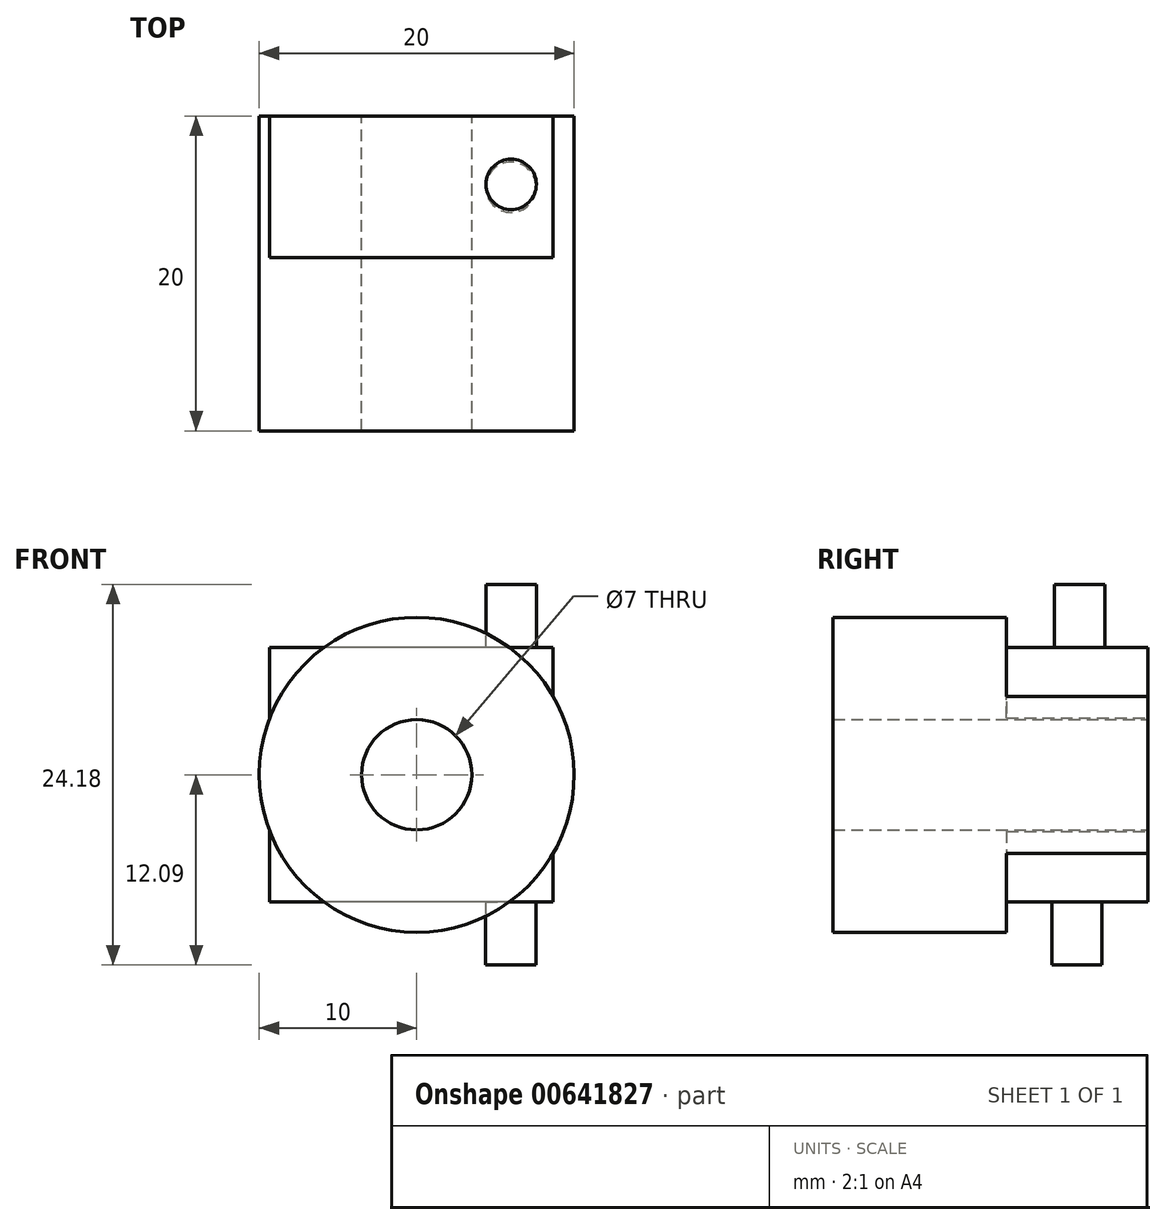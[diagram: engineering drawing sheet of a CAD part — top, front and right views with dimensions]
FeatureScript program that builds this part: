
annotation { "Feature Type Name" : "Feature", "Feature Type Description" : "" }
export const myFeature = defineFeature(function(context is Context, id is Id, definition is map)
    precondition{}
    {
        {
            var Q0;
            Q0=qCreatedBy(makeId("Front.planeOp"),FACE);
            var sketch = newSketch(context, id + "F0", { "sketchPlane" : qUnion([Q0])});
            skCircle(sketch, "E0", {"center": v(0, 0) * mm, "radius": 10 * mm});
            skCircle(sketch, "E1", {"center": v(0, 0) * mm, "radius": 3.5 * mm});
            skSolve(sketch);
        }
        {
            var Q0;
            Q0 = qSketchRegion(id + "F0", true);
            extrude(context, id + "F1", {"entities" : qUnion([Q0]), "depth" : 20 * mm, "offsetDistance" : 25 * mm});
        }
        {
            var Q0;
            Q0=qCreatedBy(makeId("Front.planeOp"),FACE);
            var sketch = newSketch(context, id + "F2", { "sketchPlane" : qUnion([Q0])});
            skLineSegment(sketch, "E2.bottom", {"start": v(8.67, 3.59) * mm, "end": v(-9.33, 3.59) * mm});
            skLineSegment(sketch, "E2.top", {"start": v(8.67, 12.09) * mm, "end": v(-9.33, 12.09) * mm});
            skLineSegment(sketch, "E2.left", {"start": v(8.67, 3.59) * mm, "end": v(8.67, 12.09) * mm});
            skLineSegment(sketch, "E2.right", {"start": v(-9.33, 3.59) * mm, "end": v(-9.33, 12.09) * mm});
            skLineSegment(sketch, "E3.MirrorCS", {"start": v(8.67, -3.59) * mm, "end": v(8.67, -12.09) * mm});
            skLineSegment(sketch, "E4.MirrorCS", {"start": v(8.67, -3.59) * mm, "end": v(-9.33, -3.59) * mm});
            skLineSegment(sketch, "E5.MirrorCS", {"start": v(8.67, -12.09) * mm, "end": v(-9.33, -12.09) * mm});
            skLineSegment(sketch, "E6.MirrorCS", {"start": v(-9.33, -3.59) * mm, "end": v(-9.33, -12.09) * mm});
            skSolve(sketch);
        }
        {
            var Q0;
            Q0=makeQuery(id+"F2.imprint","IMPRINT",FACE,{"disambiguationData":[TD([[makeQuery(id+"F2.imprint","IMPRINT",EDGE,{"derivedFrom":sQuery(id+"F2.wireOp",EDGE,"E2.bottom")}),-1.0]])]});
            var Q1;
            Q1=makeQuery(id+"F2.imprint","IMPRINT",FACE,{"disambiguationData":[TD([[makeQuery(id+"F2.imprint","IMPRINT",EDGE,{"derivedFrom":sQuery(id+"F2.wireOp",EDGE,"E3.MirrorCS")}),-1.0]])]});
            extrude(context, id + "F3", {"entities" : qUnion([Q0, Q1]), "operationType" : NewBodyOperationType.ADD, "depth" : 9 * mm, "offsetDistance" : 25 * mm});
        }
        {
            var Q0;
            Q0=makeQuery(id+"F3.opExtrude","SWEPT_FACE",FACE,{"disambiguationData":[OSD([sQuery(id+"F2.wireOp",EDGE,"E2.top")])]});
            var sketch = newSketch(context, id + "F4", { "sketchPlane" : qUnion([Q0])});
            skCircle(sketch, "E7", {"center": v(-6, -4.34) * mm, "radius": 1.6 * mm});
            skCircle(sketch, "E8.MirrorC", {"center": v(6, -4.34) * mm, "radius": 1.6 * mm});
            skSolve(sketch);
        }
        {
            var Q0;
            Q0=makeQuery(id+"F4.imprint","IMPRINT",FACE,{"disambiguationData":[TD([[makeQuery(id+"F4.imprint","IMPRINT",EDGE,{"derivedFrom":sQuery(id+"F4.wireOp",EDGE,"E7")}),1.0]])]});
            var Q1;
            Q1=makeQuery(id+"F4.imprint","IMPRINT",FACE,{"disambiguationData":[TD([[makeQuery(id+"F4.imprint","IMPRINT",EDGE,{"derivedFrom":sQuery(id+"F4.wireOp",EDGE,"E8.MirrorC")}),-1.0]])]});
            extrude(context, id + "F5", {"entities" : qUnion([Q0, Q1]), "operationType" : NewBodyOperationType.REMOVE, "oppositeDirection" : true, "depth" : 4 * mm, "offsetDistance" : 25 * mm});
        }
        {
            var Q0;
            Q0=makeQuery(id+"F3.opExtrude","SWEPT_FACE",FACE,{"disambiguationData":[OSD([sQuery(id+"F2.wireOp",EDGE,"E5.MirrorCS")])]});
            var sketch = newSketch(context, id + "F6", { "sketchPlane" : qUnion([Q0])});
            skCircle(sketch, "E9", {"center": v(-5.98, 4.52) * mm, "radius": 1.6 * mm});
            skCircle(sketch, "E10.MirrorC", {"center": v(5.98, 4.52) * mm, "radius": 1.6 * mm});
            skSolve(sketch);
        }
        {
            var Q0;
            Q0=makeQuery(id+"F6.imprint","IMPRINT",FACE,{"disambiguationData":[TD([[makeQuery(id+"F6.imprint","IMPRINT",EDGE,{"derivedFrom":sQuery(id+"F6.wireOp",EDGE,"E10.MirrorC")}),-1.0]])]});
            var Q1;
            Q1=makeQuery(id+"F6.imprint","IMPRINT",FACE,{"disambiguationData":[TD([[makeQuery(id+"F6.imprint","IMPRINT",EDGE,{"derivedFrom":sQuery(id+"F6.wireOp",EDGE,"E9")}),1.0]])]});
            extrude(context, id + "F7", {"entities" : qUnion([Q0, Q1]), "operationType" : NewBodyOperationType.REMOVE, "oppositeDirection" : true, "depth" : 4 * mm, "offsetDistance" : 25 * mm});
        }
    });
